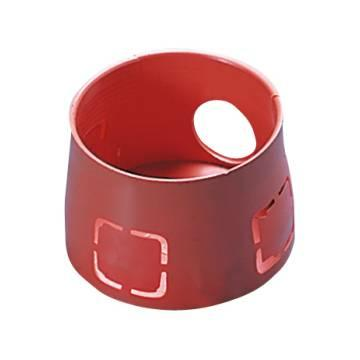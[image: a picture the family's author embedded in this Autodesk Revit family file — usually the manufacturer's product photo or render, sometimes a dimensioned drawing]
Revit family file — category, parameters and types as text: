
# Revit family: Building-ContenitoriIncasso-GEWISS-24SC-SCATOLE-INCASSO_CONICA
name_source: partatom
category: Attrezzatura elettrica
revit_build: Autodesk Revit 2016 (Build: 20161004_0715(x64)
units: mm (PartAtom-declared; Revit-internal decimal feet)

## family parameters
Condiviso = Sì
Configurazione quadro = Due colonne, circuiti in orizzontale
Host = Muro
Numero OmniClass = 23.80.30.14.24
Punto di calcolo locali = Sì
Quota connettore circolare = Usa diametro
Sempre verticale = Sì
Taglio con vuoti quando caricato = Sì
Tipo di parte = Pannello comandi
Titolo OmniClass = Junction Boxes

## types (1)
- GW24208 - Scatola rotonda conica D. 65mm
    Caratteristiche = Halogen free
    Catalogo = BUILDING
    Catalogo Serie = 24SC
    Codice EAN = 8011564016729
    Codice Electrocod = 0210
    Descrizione = SCATOLA ROTONDA CONICA D.65
    Descrizione: = Conica
    Dimensioni (mm) = Ã˜ 60x46
    Glow Wire Test = 650°C
    IDF = 0a933b5c-28d5-4203-ac42-db2cf4af8c16
    IDT = 949ec92d-8c98-491b-b93a-f1d6dc8379db
    Immagine tipo = GW24208.jpg
    Installazione = Incasso
    Modello = GW24208
    Per Pareti = Muratura
    Produttore = GEWISS S.p.A.
    SEO = Scatola
    Scheda Tecnica = https://www.gewiss.com
    Temperatura di impiego = -15 +60 °C
    Termopressione con biglia = 70 °C
    URL = https://www.gewiss.com
    Versione file RFA = 19.0
